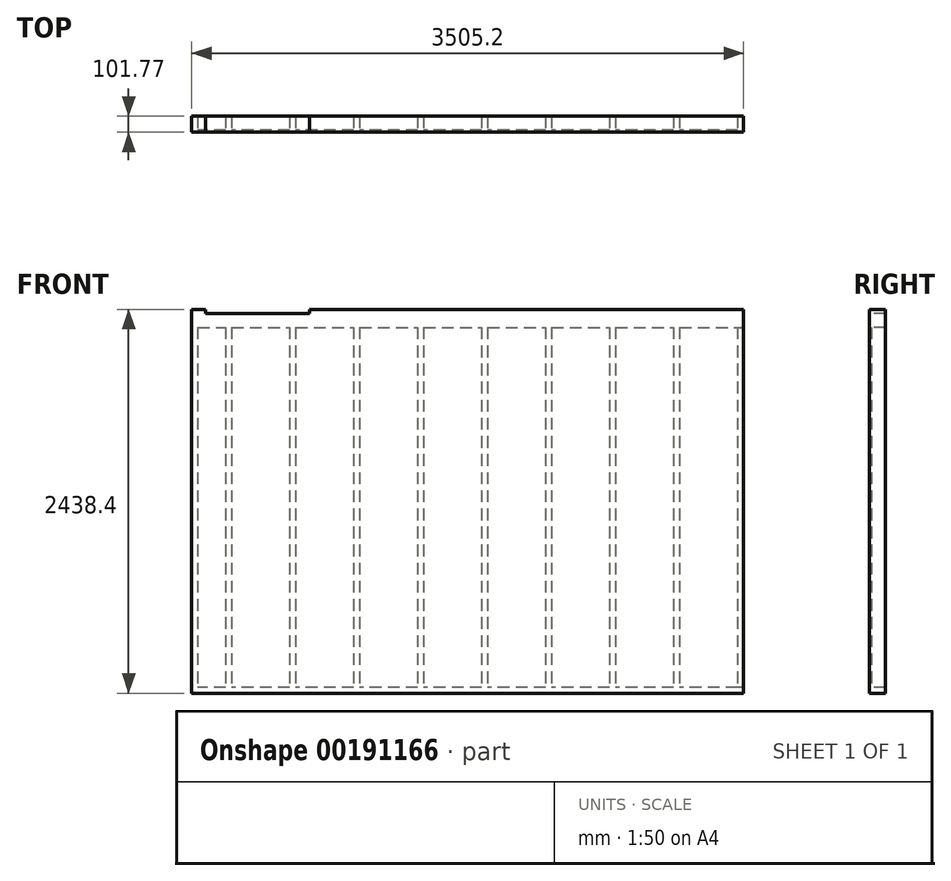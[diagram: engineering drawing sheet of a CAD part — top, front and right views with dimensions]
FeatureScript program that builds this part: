
annotation { "Feature Type Name" : "Feature", "Feature Type Description" : "" }
export const myFeature = defineFeature(function(context is Context, id is Id, definition is map)
    precondition{}
    {
        {
            var Q0;
            Q0=qCreatedBy(makeId("Top.planeOp"),FACE);
            var sketch = newSketch(context, id + "F0", { "sketchPlane" : qUnion([Q0])});
            skLineSegment(sketch, "E0.bottom", {"start": v(1752.17, -255.09) * mm, "end": v(-1753.03, -255.09) * mm});
            skLineSegment(sketch, "E0.top", {"start": v(1752.17, -166.19) * mm, "end": v(-1753.03, -166.19) * mm});
            skLineSegment(sketch, "E0.left", {"start": v(1752.17, -255.09) * mm, "end": v(1752.17, -166.19) * mm});
            skLineSegment(sketch, "E0.right", {"start": v(-1753.03, -255.09) * mm, "end": v(-1753.03, -166.19) * mm});
            skPoint(sketch, "E0.middle", {"position": v(-0.43, -210.64) * mm});
            skSolve(sketch);
        }
        {
            var Q0;
            Q0 = qSketchRegion(id + "F0", true);
            extrude(context, id + "F1", {"entities" : qUnion([Q0]), "depth" : 38.1 * mm});
        }
        {
            var Q0;
            Q0=makeQuery(id+"F1.opExtrude","CAP_FACE",FACE,{"disambiguationData":[OSD([sQuery(id+"F0.wireOp",EDGE,"E0.bottom"),sQuery(id+"F0.wireOp",EDGE,"E0.top"),sQuery(id+"F0.wireOp",EDGE,"E0.left"),sQuery(id+"F0.wireOp",EDGE,"E0.right")])],"isStart":false});
            var sketch = newSketch(context, id + "F2", { "sketchPlane" : qUnion([Q0])});
            skLineSegment(sketch, "E1.bottom", {"start": v(1752.17, -166.02) * mm, "end": v(1714.07, -166.02) * mm});
            skLineSegment(sketch, "E1.top", {"start": v(1752.17, -255.09) * mm, "end": v(1714.07, -255.09) * mm});
            skLineSegment(sketch, "E1.left", {"start": v(1752.17, -166.02) * mm, "end": v(1752.17, -255.09) * mm});
            skLineSegment(sketch, "E1.right", {"start": v(1714.07, -166.02) * mm, "end": v(1714.07, -255.09) * mm});
            skLineSegment(sketch, "E2.bottom", {"start": v(1345.77, -166.19) * mm, "end": v(1307.67, -166.19) * mm});
            skLineSegment(sketch, "E2.top", {"start": v(1345.77, -255.09) * mm, "end": v(1307.67, -255.09) * mm});
            skLineSegment(sketch, "E2.left", {"start": v(1345.77, -166.19) * mm, "end": v(1345.77, -255.09) * mm});
            skLineSegment(sketch, "E2.right", {"start": v(1307.67, -166.19) * mm, "end": v(1307.67, -255.09) * mm});
            skLineSegment(sketch, "E3.bottom", {"start": v(939.37, -166.19) * mm, "end": v(901.27, -166.19) * mm});
            skLineSegment(sketch, "E3.top", {"start": v(939.37, -255.09) * mm, "end": v(901.27, -255.09) * mm});
            skLineSegment(sketch, "E3.left", {"start": v(939.37, -166.19) * mm, "end": v(939.37, -255.09) * mm});
            skLineSegment(sketch, "E3.right", {"start": v(901.27, -166.19) * mm, "end": v(901.27, -255.09) * mm});
            skLineSegment(sketch, "E4.bottom", {"start": v(532.97, -166.19) * mm, "end": v(494.87, -166.19) * mm});
            skLineSegment(sketch, "E4.top", {"start": v(532.97, -255.09) * mm, "end": v(494.87, -255.09) * mm});
            skLineSegment(sketch, "E4.left", {"start": v(532.97, -166.19) * mm, "end": v(532.97, -255.09) * mm});
            skLineSegment(sketch, "E4.right", {"start": v(494.87, -166.19) * mm, "end": v(494.87, -255.09) * mm});
            skLineSegment(sketch, "E5.bottom", {"start": v(88.47, -166.19) * mm, "end": v(126.57, -166.19) * mm});
            skLineSegment(sketch, "E5.top", {"start": v(88.47, -255.09) * mm, "end": v(126.57, -255.09) * mm});
            skLineSegment(sketch, "E5.left", {"start": v(88.47, -166.19) * mm, "end": v(88.47, -255.09) * mm});
            skLineSegment(sketch, "E5.right", {"start": v(126.57, -166.19) * mm, "end": v(126.57, -255.09) * mm});
            skLineSegment(sketch, "E6.bottom", {"start": v(-317.93, -166.19) * mm, "end": v(-279.83, -166.19) * mm});
            skLineSegment(sketch, "E6.top", {"start": v(-317.93, -255.09) * mm, "end": v(-279.83, -255.09) * mm});
            skLineSegment(sketch, "E6.left", {"start": v(-317.93, -166.19) * mm, "end": v(-317.93, -255.09) * mm});
            skLineSegment(sketch, "E6.right", {"start": v(-279.83, -166.19) * mm, "end": v(-279.83, -255.09) * mm});
            skLineSegment(sketch, "E7.bottom", {"start": v(-724.33, -166.19) * mm, "end": v(-686.23, -166.19) * mm});
            skLineSegment(sketch, "E7.top", {"start": v(-724.33, -255.09) * mm, "end": v(-686.23, -255.09) * mm});
            skLineSegment(sketch, "E7.left", {"start": v(-724.33, -166.19) * mm, "end": v(-724.33, -255.09) * mm});
            skLineSegment(sketch, "E7.right", {"start": v(-686.23, -166.19) * mm, "end": v(-686.23, -255.09) * mm});
            skLineSegment(sketch, "E8.bottom", {"start": v(-1130.73, -166.19) * mm, "end": v(-1092.63, -166.19) * mm});
            skLineSegment(sketch, "E8.top", {"start": v(-1130.73, -255.09) * mm, "end": v(-1092.63, -255.09) * mm});
            skLineSegment(sketch, "E8.left", {"start": v(-1130.73, -166.19) * mm, "end": v(-1130.73, -255.09) * mm});
            skLineSegment(sketch, "E8.right", {"start": v(-1092.63, -166.19) * mm, "end": v(-1092.63, -255.09) * mm});
            skLineSegment(sketch, "E9.bottom", {"start": v(-1537.13, -166.19) * mm, "end": v(-1499.03, -166.19) * mm});
            skLineSegment(sketch, "E9.top", {"start": v(-1537.13, -255.09) * mm, "end": v(-1499.03, -255.09) * mm});
            skLineSegment(sketch, "E9.left", {"start": v(-1537.13, -166.19) * mm, "end": v(-1537.13, -255.09) * mm});
            skLineSegment(sketch, "E9.right", {"start": v(-1499.03, -166.19) * mm, "end": v(-1499.03, -255.09) * mm});
            skLineSegment(sketch, "E10.bottom", {"start": v(-1753.03, -166.19) * mm, "end": v(-1714.93, -166.19) * mm});
            skLineSegment(sketch, "E10.top", {"start": v(-1753.03, -255.09) * mm, "end": v(-1714.93, -255.09) * mm});
            skLineSegment(sketch, "E10.left", {"start": v(-1753.03, -166.19) * mm, "end": v(-1753.03, -255.09) * mm});
            skLineSegment(sketch, "E10.right", {"start": v(-1714.93, -166.19) * mm, "end": v(-1714.93, -255.09) * mm});
            skSolve(sketch);
        }
        {
            var Q0;
            Q0 = qSketchRegion(id + "F2", true);
            extrude(context, id + "F3", {"entities" : qUnion([Q0]), "operationType" : NewBodyOperationType.ADD, "depth" : 2286 * mm});
        }
        {
            var Q0;
            Q0=makeQuery(id+"F3.boolean.opBoolean","MERGE",FACE,{"derivedFrom":[makeQuery(id+"F1.opExtrude","SWEPT_FACE",FACE,{"disambiguationData":[OSD([sQuery(id+"F0.wireOp",EDGE,"E0.top")])]}),makeQuery(id+"F3.opExtrude","SWEPT_FACE",FACE,{"disambiguationData":[OSD([sQuery(id+"F2.wireOp",EDGE,"E2.bottom")])]}),makeQuery(id+"F3.opExtrude","SWEPT_FACE",FACE,{"disambiguationData":[OSD([sQuery(id+"F2.wireOp",EDGE,"E3.bottom")])]}),makeQuery(id+"F3.opExtrude","SWEPT_FACE",FACE,{"disambiguationData":[OSD([sQuery(id+"F2.wireOp",EDGE,"E4.bottom")])]}),makeQuery(id+"F3.opExtrude","SWEPT_FACE",FACE,{"disambiguationData":[OSD([sQuery(id+"F2.wireOp",EDGE,"E5.bottom")])]}),makeQuery(id+"F3.opExtrude","SWEPT_FACE",FACE,{"disambiguationData":[OSD([sQuery(id+"F2.wireOp",EDGE,"E6.bottom")])]}),makeQuery(id+"F3.opExtrude","SWEPT_FACE",FACE,{"disambiguationData":[OSD([sQuery(id+"F2.wireOp",EDGE,"E7.bottom")])]}),makeQuery(id+"F3.opExtrude","SWEPT_FACE",FACE,{"disambiguationData":[OSD([sQuery(id+"F2.wireOp",EDGE,"E8.bottom")])]}),makeQuery(id+"F3.opExtrude","SWEPT_FACE",FACE,{"disambiguationData":[OSD([sQuery(id+"F2.wireOp",EDGE,"E9.bottom")])]}),makeQuery(id+"F3.opExtrude","SWEPT_FACE",FACE,{"disambiguationData":[OSD([sQuery(id+"F2.wireOp",EDGE,"E10.bottom")])]})]});
            var sketch = newSketch(context, id + "F4", { "sketchPlane" : qUnion([Q0])});
            skLineSegment(sketch, "E11.bottom", {"start": v(1753.03, 2324.1) * mm, "end": v(-1752.17, 2324.1) * mm});
            skLineSegment(sketch, "E11.top", {"start": v(1753.03, 2438.4) * mm, "end": v(-1752.17, 2438.4) * mm});
            skLineSegment(sketch, "E11.left", {"start": v(1753.03, 2324.1) * mm, "end": v(1753.03, 2438.4) * mm});
            skLineSegment(sketch, "E11.right", {"start": v(-1752.17, 2324.1) * mm, "end": v(-1752.17, 2438.4) * mm});
            skSolve(sketch);
        }
        {
            var Q0;
            Q0 = qSketchRegion(id + "F4", true);
            extrude(context, id + "F5", {"entities" : qUnion([Q0]), "operationType" : NewBodyOperationType.ADD, "oppositeDirection" : true, "depth" : 88.9 * mm});
        }
        {
            var Q0;
            Q0=makeQuery(id+"F5.boolean.opBoolean","MERGE",FACE,{"derivedFrom":[makeQuery(id+"F3.boolean.opBoolean","MERGE",FACE,{"derivedFrom":[makeQuery(id+"F1.opExtrude","SWEPT_FACE",FACE,{"disambiguationData":[OSD([sQuery(id+"F0.wireOp",EDGE,"E0.bottom")])]}),makeQuery(id+"F3.opExtrude","SWEPT_FACE",FACE,{"disambiguationData":[OSD([sQuery(id+"F2.wireOp",EDGE,"E1.top")])]}),makeQuery(id+"F3.opExtrude","SWEPT_FACE",FACE,{"disambiguationData":[OSD([sQuery(id+"F2.wireOp",EDGE,"E2.top")])]}),makeQuery(id+"F3.opExtrude","SWEPT_FACE",FACE,{"disambiguationData":[OSD([sQuery(id+"F2.wireOp",EDGE,"E3.top")])]}),makeQuery(id+"F3.opExtrude","SWEPT_FACE",FACE,{"disambiguationData":[OSD([sQuery(id+"F2.wireOp",EDGE,"E4.top")])]}),makeQuery(id+"F3.opExtrude","SWEPT_FACE",FACE,{"disambiguationData":[OSD([sQuery(id+"F2.wireOp",EDGE,"E5.top")])]}),makeQuery(id+"F3.opExtrude","SWEPT_FACE",FACE,{"disambiguationData":[OSD([sQuery(id+"F2.wireOp",EDGE,"E6.top")])]}),makeQuery(id+"F3.opExtrude","SWEPT_FACE",FACE,{"disambiguationData":[OSD([sQuery(id+"F2.wireOp",EDGE,"E7.top")])]}),makeQuery(id+"F3.opExtrude","SWEPT_FACE",FACE,{"disambiguationData":[OSD([sQuery(id+"F2.wireOp",EDGE,"E8.top")])]}),makeQuery(id+"F3.opExtrude","SWEPT_FACE",FACE,{"disambiguationData":[OSD([sQuery(id+"F2.wireOp",EDGE,"E9.top")])]}),makeQuery(id+"F3.opExtrude","SWEPT_FACE",FACE,{"disambiguationData":[OSD([sQuery(id+"F2.wireOp",EDGE,"E10.top")])]})]}),makeQuery(id+"F5.opExtrude","CAP_FACE",FACE,{"disambiguationData":[OSD([sQuery(id+"F4.wireOp",EDGE,"E11.bottom"),sQuery(id+"F4.wireOp",EDGE,"E11.top"),sQuery(id+"F4.wireOp",EDGE,"E11.left"),sQuery(id+"F4.wireOp",EDGE,"E11.right")])],"isStart":false})]});
            var sketch = newSketch(context, id + "F6", { "sketchPlane" : qUnion([Q0])});
            skLineSegment(sketch, "E12.bottom", {"start": v(-1753.03, 2438.4) * mm, "end": v(1752.17, 2438.4) * mm});
            skLineSegment(sketch, "E12.top", {"start": v(-1753.03, 0) * mm, "end": v(1752.17, 0) * mm});
            skLineSegment(sketch, "E12.left", {"start": v(-1753.03, 2438.4) * mm, "end": v(-1753.03, 0) * mm});
            skLineSegment(sketch, "E12.right", {"start": v(1752.17, 2438.4) * mm, "end": v(1752.17, 0) * mm});
            skSolve(sketch);
        }
        {
            var Q0;
            Q0 = qSketchRegion(id + "F6", true);
            extrude(context, id + "F7", {"entities" : qUnion([Q0]), "operationType" : NewBodyOperationType.ADD, "depth" : 12.7 * mm});
        }
        {
            var Q0;
            Q0=makeQuery(id+"F7.opExtrude","CAP_FACE",FACE,{"disambiguationData":[OSD([sQuery(id+"F6.wireOp",EDGE,"E12.bottom"),sQuery(id+"F6.wireOp",EDGE,"E12.top"),sQuery(id+"F6.wireOp",EDGE,"E12.left"),sQuery(id+"F6.wireOp",EDGE,"E12.right")])],"isStart":false});
            var sketch = newSketch(context, id + "F8", { "sketchPlane" : qUnion([Q0])});
            skLineSegment(sketch, "E13.bottom", {"start": v(-1664.13, 2438.4) * mm, "end": v(-1003.73, 2438.4) * mm});
            skLineSegment(sketch, "E13.top", {"start": v(-1664.13, 2413) * mm, "end": v(-1003.73, 2413) * mm});
            skLineSegment(sketch, "E13.left", {"start": v(-1664.13, 2438.4) * mm, "end": v(-1664.13, 2413) * mm});
            skLineSegment(sketch, "E13.right", {"start": v(-1003.73, 2438.4) * mm, "end": v(-1003.73, 2413) * mm});
            skSolve(sketch);
        }
        {
            var Q0;
            Q0 = qSketchRegion(id + "F8", true);
            extrude(context, id + "F9", {"entities" : qUnion([Q0]), "operationType" : NewBodyOperationType.REMOVE, "oppositeDirection" : true, "depth" : 132.08 * mm});
        }
    });
